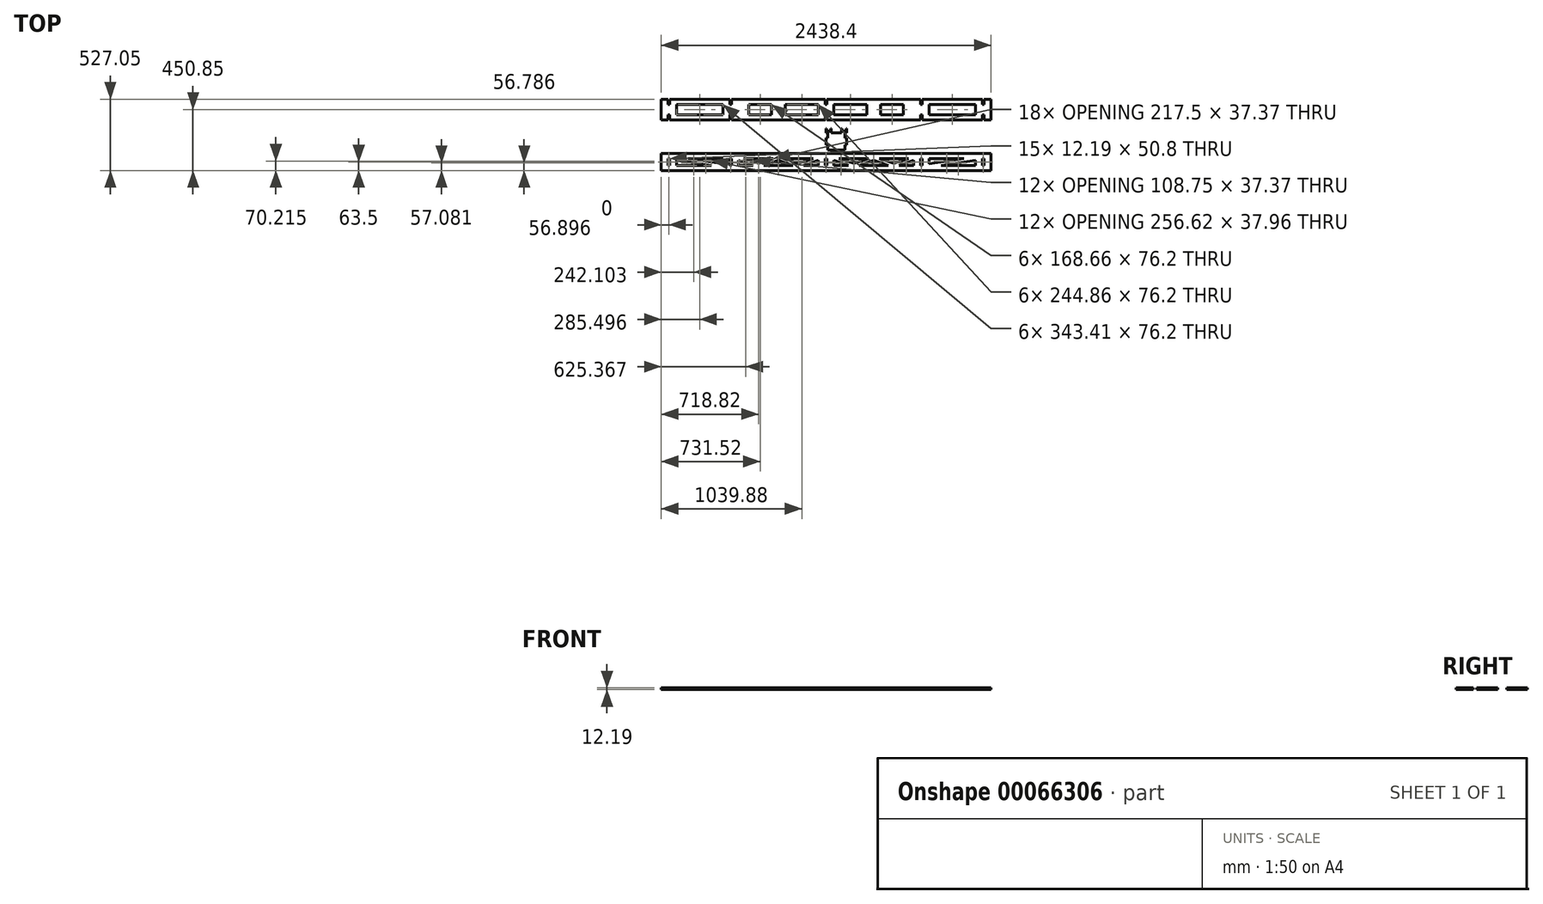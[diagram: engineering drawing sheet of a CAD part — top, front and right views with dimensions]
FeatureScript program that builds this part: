
annotation { "Feature Type Name" : "Feature", "Feature Type Description" : "" }
export const myFeature = defineFeature(function(context is Context, id is Id, definition is map)
    precondition{}
    {
        {
            var Q0;
            Q0=qCreatedBy(makeId("Top.planeOp"),FACE);
            var sketch = newSketch(context, id + "F0", { "sketchPlane" : qUnion([Q0])});
            skLineSegment(sketch, "E0.bottom", {"start": v(-1219.2, 44.45) * mm, "end": v(1219.2, 44.45) * mm});
            skLineSegment(sketch, "E0.top", {"start": v(-1219.2, -107.95) * mm, "end": v(1219.2, -107.95) * mm});
            skLineSegment(sketch, "E0.left", {"start": v(-1219.2, 44.45) * mm, "end": v(-1219.2, -107.95) * mm});
            skLineSegment(sketch, "E0.right", {"start": v(1219.2, 44.45) * mm, "end": v(1219.2, -107.95) * mm});
            skLineSegment(sketch, "E1", {"start": v(0, 44.45) * mm, "end": v(0, -107.95) * mm, "construction": true});
            skLineSegment(sketch, "E2.0", {"start": v(-6.1, 44.45) * mm, "end": v(-6.1, 6.35) * mm});
            skLineSegment(sketch, "E3.MirrorCS", {"start": v(6.1, 44.45) * mm, "end": v(6.1, 6.35) * mm});
            skLineSegment(sketch, "E4", {"start": v(-1219.2, -31.75) * mm, "end": v(-1168.4, -31.75) * mm, "construction": true});
            skLineSegment(sketch, "E5", {"start": v(-1219.2, -31.75) * mm, "end": v(-711.2, -31.75) * mm, "construction": true});
            skLineSegment(sketch, "E6", {"start": v(-711.2, 44.45) * mm, "end": v(-711.2, 6.35) * mm});
            skLineSegment(sketch, "E7", {"start": v(-1168.4, 44.45) * mm, "end": v(-1168.4, 6.35) * mm});
            skLineSegment(sketch, "E8.0", {"start": v(-1156.2, 44.45) * mm, "end": v(-1156.2, 6.35) * mm});
            skLineSegment(sketch, "E9.0", {"start": v(-699, 44.45) * mm, "end": v(-699, 6.35) * mm});
            skLineSegment(sketch, "E10.MirrorCS", {"start": v(699, 44.45) * mm, "end": v(699, 6.35) * mm});
            skLineSegment(sketch, "E11.MirrorCS", {"start": v(711.2, 44.45) * mm, "end": v(711.2, 6.35) * mm});
            skLineSegment(sketch, "E12.MirrorCS", {"start": v(1168.4, 44.45) * mm, "end": v(1168.4, 6.35) * mm});
            skLineSegment(sketch, "E13.MirrorCS", {"start": v(1156.2, 44.45) * mm, "end": v(1156.2, 6.35) * mm});
            skLineSegment(sketch, "E14", {"start": v(-1219.2, -31.75) * mm, "end": v(1219.2, -31.75) * mm, "construction": true});
            skLineSegment(sketch, "E15.0", {"start": v(-1219.2, 6.35) * mm, "end": v(1219.2, 6.35) * mm, "construction": true});
            skLineSegment(sketch, "E16.MirrorCS", {"start": v(-1219.2, -69.85) * mm, "end": v(1219.2, -69.85) * mm, "construction": true});
            skLineSegment(sketch, "E17", {"start": v(-1168.4, 6.35) * mm, "end": v(-1156.2, 6.35) * mm});
            skLineSegment(sketch, "E18", {"start": v(-711.2, 6.35) * mm, "end": v(-699, 6.35) * mm});
            skLineSegment(sketch, "E19", {"start": v(-6.1, 6.35) * mm, "end": v(6.1, 6.35) * mm});
            skLineSegment(sketch, "E20.MirrorCS", {"start": v(1168.4, 6.35) * mm, "end": v(1156.2, 6.35) * mm});
            skLineSegment(sketch, "E21.MirrorCS", {"start": v(711.2, 6.35) * mm, "end": v(699, 6.35) * mm});
            skLineSegment(sketch, "E22.MirrorCS", {"start": v(1168.4, -69.85) * mm, "end": v(1156.2, -69.85) * mm});
            skLineSegment(sketch, "E23.MirrorCS", {"start": v(-1168.4, -69.85) * mm, "end": v(-1156.2, -69.85) * mm});
            skLineSegment(sketch, "E24.MirrorCS", {"start": v(-6.1, -69.85) * mm, "end": v(6.1, -69.85) * mm});
            skLineSegment(sketch, "E25.MirrorCS", {"start": v(-711.2, -69.85) * mm, "end": v(-699, -69.85) * mm});
            skLineSegment(sketch, "E26.MirrorCS", {"start": v(711.2, -69.85) * mm, "end": v(699, -69.85) * mm});
            skLineSegment(sketch, "E27.0", {"start": v(-1105.4, 6.35) * mm, "end": v(-1105.4, -69.85) * mm});
            skLineSegment(sketch, "E28.0", {"start": v(-762, 6.35) * mm, "end": v(-762, -69.85) * mm});
            skLineSegment(sketch, "E29.0", {"start": v(-648.2, 6.35) * mm, "end": v(-648.2, -69.85) * mm, "construction": true});
            skLineSegment(sketch, "E30.0", {"start": v(-56.9, 6.35) * mm, "end": v(-56.9, -69.85) * mm});
            skLineSegment(sketch, "E31.0", {"start": v(56.9, 6.35) * mm, "end": v(56.9, -69.85) * mm});
            skLineSegment(sketch, "E32.0", {"start": v(648.2, 6.35) * mm, "end": v(648.2, -69.85) * mm});
            skLineSegment(sketch, "E33.0", {"start": v(762, 6.35) * mm, "end": v(762, -69.85) * mm});
            skLineSegment(sketch, "E34.0", {"start": v(1105.4, 6.35) * mm, "end": v(1105.4, -69.85) * mm});
            skLineSegment(sketch, "E35", {"start": v(-699, 110.18) * mm, "end": v(-6.1, 110.18) * mm, "construction": true});
            skLineSegment(sketch, "E36", {"start": v(-352.55, -69.85) * mm, "end": v(-352.55, 6.35) * mm, "construction": true});
            skPoint(sketch, "E36.startSnap0", {"position": v(-352.55, 110.18) * mm});
            skLineSegment(sketch, "E37.0", {"start": v(-403.35, -69.85) * mm, "end": v(-403.35, 6.35) * mm});
            skLineSegment(sketch, "E38.0", {"start": v(-301.75, -69.85) * mm, "end": v(-301.75, 6.35) * mm});
            skLineSegment(sketch, "E39", {"start": v(-1105.4, 6.35) * mm, "end": v(-762, 6.35) * mm});
            skLineSegment(sketch, "E40", {"start": v(-762, -69.85) * mm, "end": v(-1105.4, -69.85) * mm});
            skLineSegment(sketch, "E41", {"start": v(-648.2, 6.35) * mm, "end": v(-572, 6.35) * mm, "construction": true});
            skLineSegment(sketch, "E42", {"start": v(-301.75, 6.35) * mm, "end": v(-56.9, 6.35) * mm});
            skLineSegment(sketch, "E43", {"start": v(-56.9, -69.85) * mm, "end": v(-301.75, -69.85) * mm});
            skLineSegment(sketch, "E44", {"start": v(-403.35, -69.85) * mm, "end": v(-572, -69.85) * mm});
            skLineSegment(sketch, "E45.MirrorCS", {"start": v(403.35, -69.85) * mm, "end": v(648.2, -69.85) * mm});
            skLineSegment(sketch, "E46.MirrorCS", {"start": v(56.9, -69.85) * mm, "end": v(301.75, -69.85) * mm});
            skLineSegment(sketch, "E47.MirrorCS", {"start": v(301.75, 6.35) * mm, "end": v(56.9, 6.35) * mm});
            skLineSegment(sketch, "E48.MirrorCS", {"start": v(301.75, -69.85) * mm, "end": v(301.75, 6.35) * mm});
            skLineSegment(sketch, "E49.MirrorCS", {"start": v(403.35, -69.85) * mm, "end": v(403.35, 6.35) * mm});
            skLineSegment(sketch, "E50.MirrorCS", {"start": v(648.2, 6.35) * mm, "end": v(403.35, 6.35) * mm});
            skLineSegment(sketch, "E51.MirrorCS", {"start": v(1105.4, 6.35) * mm, "end": v(762, 6.35) * mm});
            skLineSegment(sketch, "E52.MirrorCS", {"start": v(762, -69.85) * mm, "end": v(1105.4, -69.85) * mm});
            skLineSegment(sketch, "E53.trimOffspring", {"start": v(699, -69.85) * mm, "end": v(699, -107.95) * mm});
            skLineSegment(sketch, "E54.trimOffspring", {"start": v(711.2, -69.85) * mm, "end": v(711.2, -107.95) * mm});
            skLineSegment(sketch, "E55.trimOffspring", {"start": v(1156.2, -69.85) * mm, "end": v(1156.2, -107.95) * mm});
            skLineSegment(sketch, "E56.trimOffspring", {"start": v(1168.4, -69.85) * mm, "end": v(1168.4, -107.95) * mm});
            skLineSegment(sketch, "E57.trimOffspring", {"start": v(-6.1, -69.85) * mm, "end": v(-6.1, -107.95) * mm});
            skLineSegment(sketch, "E58.trimOffspring", {"start": v(6.1, -69.85) * mm, "end": v(6.1, -107.95) * mm});
            skLineSegment(sketch, "E59.trimOffspring", {"start": v(-1168.4, -69.85) * mm, "end": v(-1168.4, -107.95) * mm});
            skLineSegment(sketch, "E60.trimOffspring", {"start": v(-1156.2, -69.85) * mm, "end": v(-1156.2, -107.95) * mm});
            skLineSegment(sketch, "E61.trimOffspring", {"start": v(-711.2, -69.85) * mm, "end": v(-711.2, -107.95) * mm});
            skLineSegment(sketch, "E62.trimOffspring", {"start": v(-699, -69.85) * mm, "end": v(-699, -107.95) * mm});
            skLineSegment(sketch, "E63.bottom", {"start": v(38.1, -203.2) * mm, "end": v(114.3, -203.2) * mm});
            skLineSegment(sketch, "E63.top", {"start": v(12.2, -330.2) * mm, "end": v(140.2, -330.2) * mm});
            skLineSegment(sketch, "E63.left", {"start": v(0, -241.3) * mm, "end": v(0, -292.1) * mm});
            skLineSegment(sketch, "E63.right", {"start": v(152.4, -241.3) * mm, "end": v(152.4, -292.1) * mm});
            skLineSegment(sketch, "E64.top", {"start": v(0, -174.18) * mm, "end": v(2.22, -174.18) * mm});
            skLineSegment(sketch, "E64.left", {"start": v(0, -203.2) * mm, "end": v(0, -174.18) * mm});
            skLineSegment(sketch, "E64.right", {"start": v(38.1, -203.2) * mm, "end": v(38.1, -174.18) * mm});
            skArc(sketch, "E65", {"start": v(2.22, -174.18) * mm, "mid": v(19.05, -191) * mm, "end": v(35.88, -174.18) * mm});
            skLineSegment(sketch, "E66.trimOffspring", {"start": v(35.88, -174.18) * mm, "end": v(38.1, -174.18) * mm});
            skLineSegment(sketch, "E67.bottom", {"start": v(0, -203.2) * mm, "end": v(12.2, -203.2) * mm});
            skLineSegment(sketch, "E67.top", {"start": v(0, -241.3) * mm, "end": v(12.2, -241.3) * mm});
            skLineSegment(sketch, "E67.right", {"start": v(12.2, -203.2) * mm, "end": v(12.2, -241.3) * mm});
            skLineSegment(sketch, "E68", {"start": v(0, -266.7) * mm, "end": v(152.4, -266.7) * mm, "construction": true});
            skLineSegment(sketch, "E69", {"start": v(152.4, -266.7) * mm, "end": v(76.2, -330.2) * mm, "construction": true});
            skLineSegment(sketch, "E70", {"start": v(76.2, -330.2) * mm, "end": v(76.2, -203.2) * mm, "construction": true});
            skLineSegment(sketch, "E71.MirrorCS", {"start": v(12.2, -330.2) * mm, "end": v(12.2, -292.1) * mm});
            skLineSegment(sketch, "E72.MirrorCS", {"start": v(0, -292.1) * mm, "end": v(12.2, -292.1) * mm});
            skLineSegment(sketch, "E73.MirrorCS", {"start": v(152.4, -203.2) * mm, "end": v(140.2, -203.2) * mm});
            skLineSegment(sketch, "E74.MirrorCS", {"start": v(140.2, -330.2) * mm, "end": v(140.2, -292.1) * mm});
            skLineSegment(sketch, "E75.MirrorCS", {"start": v(152.4, -241.3) * mm, "end": v(140.2, -241.3) * mm});
            skLineSegment(sketch, "E76.MirrorCS", {"start": v(140.2, -203.2) * mm, "end": v(140.2, -241.3) * mm});
            skLineSegment(sketch, "E77.MirrorCS", {"start": v(152.4, -292.1) * mm, "end": v(140.2, -292.1) * mm});
            skLineSegment(sketch, "E78.MirrorCS", {"start": v(114.3, -203.2) * mm, "end": v(114.3, -174.18) * mm});
            skArc(sketch, "E79.MirrorCS", {"start": v(150.18, -174.18) * mm, "mid": v(133.35, -191) * mm, "end": v(116.52, -174.18) * mm});
            skLineSegment(sketch, "E80.MirrorCS", {"start": v(116.52, -174.18) * mm, "end": v(114.3, -174.18) * mm});
            skLineSegment(sketch, "E81.MirrorCS", {"start": v(152.4, -174.18) * mm, "end": v(150.18, -174.18) * mm});
            skLineSegment(sketch, "E82.MirrorCS", {"start": v(152.4, -203.2) * mm, "end": v(152.4, -174.18) * mm});
            skPoint(sketch, "E83.MirrorCS.start.orphan", {"position": v(0, -330.2) * mm});
            skPoint(sketch, "E84.trimOffspring.end.orphan", {"position": v(152.4, -203.2) * mm});
            skPoint(sketch, "E85.MirrorCS.start.orphan", {"position": v(152.4, -330.2) * mm});
            skLineSegment(sketch, "E86.bottom", {"start": v(-1219.2, -355.6) * mm, "end": v(1219.2, -355.6) * mm});
            skLineSegment(sketch, "E86.top", {"start": v(-1219.2, -482.6) * mm, "end": v(1219.2, -482.6) * mm});
            skLineSegment(sketch, "E86.left", {"start": v(-1219.2, -355.6) * mm, "end": v(-1219.2, -482.6) * mm});
            skLineSegment(sketch, "E86.right", {"start": v(1219.2, -355.6) * mm, "end": v(1219.2, -482.6) * mm});
            skLineSegment(sketch, "E87.bottom", {"start": v(-1168.4, -355.6) * mm, "end": v(-1156.2, -355.6) * mm, "construction": true});
            skLineSegment(sketch, "E87.top", {"start": v(-1168.4, -393.7) * mm, "end": v(-1156.2, -393.7) * mm});
            skLineSegment(sketch, "E87.left", {"start": v(-1168.4, -355.6) * mm, "end": v(-1168.4, -393.7) * mm, "construction": true});
            skLineSegment(sketch, "E87.right", {"start": v(-1156.2, -355.6) * mm, "end": v(-1156.2, -393.7) * mm, "construction": true});
            skLineSegment(sketch, "E88", {"start": v(-1168.4, -393.7) * mm, "end": v(-1168.4, -444.5) * mm});
            skLineSegment(sketch, "E89", {"start": v(-1168.4, -444.5) * mm, "end": v(-1156.2, -444.5) * mm});
            skLineSegment(sketch, "E90", {"start": v(-1156.2, -444.5) * mm, "end": v(-1156.2, -393.7) * mm});
            skLineSegment(sketch, "E91", {"start": v(-1156.2, -241.75) * mm, "end": v(-711.2, -241.75) * mm, "construction": true});
            skLineSegment(sketch, "E92", {"start": v(-933.7, -241.75) * mm, "end": v(-933.7, -204.74) * mm, "construction": true});
            skLineSegment(sketch, "E93", {"start": v(-699, -247.2) * mm, "end": v(-6.1, -247.2) * mm, "construction": true});
            skLineSegment(sketch, "E94", {"start": v(-352.55, -247.2) * mm, "end": v(-352.55, -185.08) * mm, "construction": true});
            skLineSegment(sketch, "E95.MirrorCS", {"start": v(-699, -393.7) * mm, "end": v(-711.2, -393.7) * mm});
            skLineSegment(sketch, "E96.MirrorCS", {"start": v(-699, -393.7) * mm, "end": v(-699, -444.5) * mm});
            skLineSegment(sketch, "E97.MirrorCS", {"start": v(-711.2, -444.5) * mm, "end": v(-711.2, -393.7) * mm});
            skLineSegment(sketch, "E98.MirrorCS", {"start": v(-699, -444.5) * mm, "end": v(-711.2, -444.5) * mm});
            skLineSegment(sketch, "E99.MirrorCS", {"start": v(-6.1, -444.5) * mm, "end": v(6.1, -444.5) * mm});
            skLineSegment(sketch, "E100.MirrorCS", {"start": v(-6.1, -393.7) * mm, "end": v(6.1, -393.7) * mm});
            skLineSegment(sketch, "E101.MirrorCS", {"start": v(-6.1, -393.7) * mm, "end": v(-6.1, -444.5) * mm});
            skLineSegment(sketch, "E102.MirrorCS", {"start": v(6.1, -444.5) * mm, "end": v(6.1, -393.7) * mm});
            skLineSegment(sketch, "E103.MirrorCS", {"start": v(1168.4, -393.7) * mm, "end": v(1156.2, -393.7) * mm});
            skLineSegment(sketch, "E104.MirrorCS", {"start": v(1168.4, -393.7) * mm, "end": v(1168.4, -444.5) * mm});
            skLineSegment(sketch, "E105.MirrorCS", {"start": v(1168.4, -444.5) * mm, "end": v(1156.2, -444.5) * mm});
            skLineSegment(sketch, "E106.MirrorCS", {"start": v(1156.2, -444.5) * mm, "end": v(1156.2, -393.7) * mm});
            skLineSegment(sketch, "E107.MirrorCS", {"start": v(699, -444.5) * mm, "end": v(711.2, -444.5) * mm});
            skLineSegment(sketch, "E108.MirrorCS", {"start": v(699, -393.7) * mm, "end": v(711.2, -393.7) * mm});
            skLineSegment(sketch, "E109.MirrorCS", {"start": v(711.2, -444.5) * mm, "end": v(711.2, -393.7) * mm});
            skLineSegment(sketch, "E110.MirrorCS", {"start": v(699, -393.7) * mm, "end": v(699, -444.5) * mm});
            skLineSegment(sketch, "E111", {"start": v(-1018.62, -393.7) * mm, "end": v(-762, -393.7) * mm});
            skLineSegment(sketch, "E112", {"start": v(-762, -393.7) * mm, "end": v(-762, -431.66) * mm});
            skLineSegment(sketch, "E113", {"start": v(-848.79, -444.5) * mm, "end": v(-1105.4, -444.5) * mm});
            skLineSegment(sketch, "E114", {"start": v(-1105.4, -444.5) * mm, "end": v(-1105.4, -406.54) * mm});
            skLineSegment(sketch, "E115", {"start": v(-648.2, -407.13) * mm, "end": v(-648.2, -444.5) * mm});
            skLineSegment(sketch, "E116", {"start": v(-648.2, -444.5) * mm, "end": v(-539.46, -444.5) * mm});
            skLineSegment(sketch, "E117", {"start": v(-56.9, -444.5) * mm, "end": v(-56.9, -407.13) * mm});
            skLineSegment(sketch, "E118", {"start": v(-95.97, -393.7) * mm, "end": v(-313.47, -393.7) * mm});
            skLineSegment(sketch, "E119", {"start": v(-1105.4, -393.7) * mm, "end": v(-762, -444.5) * mm, "construction": true});
            skPoint(sketch, "E120.endSnap0", {"position": v(-525.78, -69.85) * mm});
            skPoint(sketch, "E121.endSnap0", {"position": v(-179.32, -69.85) * mm});
            skLineSegment(sketch, "E122", {"start": v(-352.55, -393.7) * mm, "end": v(-352.55, -444.5) * mm, "construction": true});
            skLineSegment(sketch, "E123", {"start": v(-352.55, -444.5) * mm, "end": v(-243.8, -444.5) * mm});
            skLineSegment(sketch, "E124", {"start": v(-648.2, -393.7) * mm, "end": v(-500.38, -444.5) * mm, "construction": true});
            skLineSegment(sketch, "E125", {"start": v(-500.38, -444.5) * mm, "end": v(-352.55, -393.7) * mm, "construction": true});
            skLineSegment(sketch, "E126", {"start": v(-352.55, -393.7) * mm, "end": v(-204.72, -444.5) * mm, "construction": true});
            skLineSegment(sketch, "E127", {"start": v(-204.72, -444.5) * mm, "end": v(-56.9, -393.7) * mm, "construction": true});
            skLineSegment(sketch, "E128.0", {"start": v(-1105.4, -406.54) * mm, "end": v(-848.79, -444.5) * mm});
            skLineSegment(sketch, "E129.0", {"start": v(-1018.62, -393.7) * mm, "end": v(-762, -431.66) * mm});
            skLineSegment(sketch, "E130.0", {"start": v(-609.13, -393.7) * mm, "end": v(-500.38, -431.07) * mm});
            skLineSegment(sketch, "E131.0", {"start": v(-648.2, -407.13) * mm, "end": v(-539.46, -444.5) * mm});
            skLineSegment(sketch, "E132.0", {"start": v(-500.38, -431.07) * mm, "end": v(-391.63, -393.7) * mm});
            skLineSegment(sketch, "E133.0", {"start": v(-461.3, -444.5) * mm, "end": v(-352.55, -407.13) * mm});
            skLineSegment(sketch, "E134.0", {"start": v(-313.47, -393.7) * mm, "end": v(-204.72, -431.07) * mm});
            skLineSegment(sketch, "E135.0", {"start": v(-352.55, -407.13) * mm, "end": v(-243.8, -444.5) * mm});
            skLineSegment(sketch, "E136.0", {"start": v(-204.72, -431.07) * mm, "end": v(-95.97, -393.7) * mm});
            skLineSegment(sketch, "E137.0", {"start": v(-165.65, -444.5) * mm, "end": v(-56.9, -407.13) * mm});
            skLineSegment(sketch, "E138.trimOffspring", {"start": v(-461.3, -444.5) * mm, "end": v(-352.55, -444.5) * mm});
            skLineSegment(sketch, "E139.trimOffspring", {"start": v(-165.65, -444.5) * mm, "end": v(-56.9, -444.5) * mm});
            skLineSegment(sketch, "E140.trimOffspring", {"start": v(-391.63, -393.7) * mm, "end": v(-609.13, -393.7) * mm});
            skLineSegment(sketch, "E141.MirrorCS", {"start": v(56.9, -444.5) * mm, "end": v(56.9, -407.13) * mm});
            skLineSegment(sketch, "E142.MirrorCS", {"start": v(313.47, -393.7) * mm, "end": v(204.72, -431.07) * mm});
            skLineSegment(sketch, "E143.MirrorCS", {"start": v(648.2, -444.5) * mm, "end": v(539.46, -444.5) * mm});
            skLineSegment(sketch, "E144.MirrorCS", {"start": v(165.65, -444.5) * mm, "end": v(56.9, -407.13) * mm});
            skLineSegment(sketch, "E145.MirrorCS", {"start": v(95.97, -393.7) * mm, "end": v(313.47, -393.7) * mm});
            skLineSegment(sketch, "E146.MirrorCS", {"start": v(204.72, -431.07) * mm, "end": v(95.97, -393.7) * mm});
            skLineSegment(sketch, "E147.MirrorCS", {"start": v(461.3, -444.5) * mm, "end": v(352.55, -444.5) * mm});
            skLineSegment(sketch, "E148.MirrorCS", {"start": v(352.55, -393.7) * mm, "end": v(352.55, -444.5) * mm, "construction": true});
            skLineSegment(sketch, "E149.MirrorCS", {"start": v(204.72, -444.5) * mm, "end": v(56.9, -393.7) * mm, "construction": true});
            skLineSegment(sketch, "E150.MirrorCS", {"start": v(648.2, -407.13) * mm, "end": v(648.2, -444.5) * mm});
            skLineSegment(sketch, "E151.MirrorCS", {"start": v(461.3, -444.5) * mm, "end": v(352.55, -407.13) * mm});
            skLineSegment(sketch, "E152.MirrorCS", {"start": v(352.55, -393.7) * mm, "end": v(204.72, -444.5) * mm, "construction": true});
            skLineSegment(sketch, "E153.MirrorCS", {"start": v(165.65, -444.5) * mm, "end": v(56.9, -444.5) * mm});
            skLineSegment(sketch, "E154.MirrorCS", {"start": v(352.55, -444.5) * mm, "end": v(243.8, -444.5) * mm});
            skLineSegment(sketch, "E155.MirrorCS", {"start": v(500.38, -431.07) * mm, "end": v(391.63, -393.7) * mm});
            skLineSegment(sketch, "E156.MirrorCS", {"start": v(352.55, -407.13) * mm, "end": v(243.8, -444.5) * mm});
            skLineSegment(sketch, "E157.MirrorCS", {"start": v(609.13, -393.7) * mm, "end": v(500.38, -431.07) * mm});
            skLineSegment(sketch, "E158.MirrorCS", {"start": v(391.63, -393.7) * mm, "end": v(609.13, -393.7) * mm});
            skLineSegment(sketch, "E159.MirrorCS", {"start": v(648.2, -393.7) * mm, "end": v(500.38, -444.5) * mm, "construction": true});
            skLineSegment(sketch, "E160.MirrorCS", {"start": v(648.2, -407.13) * mm, "end": v(539.46, -444.5) * mm});
            skLineSegment(sketch, "E161.MirrorCS", {"start": v(1105.4, -393.7) * mm, "end": v(762, -444.5) * mm, "construction": true});
            skLineSegment(sketch, "E162.MirrorCS", {"start": v(500.38, -444.5) * mm, "end": v(352.55, -393.7) * mm, "construction": true});
            skLineSegment(sketch, "E163.MirrorCS", {"start": v(1105.4, -406.54) * mm, "end": v(848.79, -444.5) * mm});
            skLineSegment(sketch, "E164.MirrorCS", {"start": v(1105.4, -444.5) * mm, "end": v(1105.4, -406.54) * mm});
            skLineSegment(sketch, "E165.MirrorCS", {"start": v(1018.62, -393.7) * mm, "end": v(762, -393.7) * mm});
            skLineSegment(sketch, "E166.MirrorCS", {"start": v(762, -393.7) * mm, "end": v(762, -431.66) * mm});
            skLineSegment(sketch, "E167.MirrorCS", {"start": v(1018.62, -393.7) * mm, "end": v(762, -431.66) * mm});
            skLineSegment(sketch, "E168.MirrorCS", {"start": v(848.79, -444.5) * mm, "end": v(1105.4, -444.5) * mm});
            skLineSegment(sketch, "E169.bottom", {"start": v(-1219.2, 508) * mm, "end": v(1219.2, 508) * mm});
            skLineSegment(sketch, "E169.top", {"start": v(-1219.2, -711.2) * mm, "end": v(1219.2, -711.2) * mm});
            skLineSegment(sketch, "E169.left", {"start": v(-1219.2, 508) * mm, "end": v(-1219.2, -711.2) * mm});
            skLineSegment(sketch, "E169.right", {"start": v(1219.2, 508) * mm, "end": v(1219.2, -711.2) * mm});
            skLineSegment(sketch, "E170.top", {"start": v(-648.2, -69.85) * mm, "end": v(-572, -69.85) * mm, "construction": true});
            skLineSegment(sketch, "E170.right", {"start": v(-572, 6.35) * mm, "end": v(-572, -69.85) * mm});
            skLineSegment(sketch, "E171", {"start": v(-572, 6.35) * mm, "end": v(-403.35, 6.35) * mm});
            skLineSegment(sketch, "E172", {"start": v(-572, -69.85) * mm, "end": v(-648.2, -69.85) * mm, "construction": true});
            skLineSegment(sketch, "E173.bottom", {"start": v(648.2, 6.35) * mm, "end": v(572, 6.35) * mm, "construction": true});
            skLineSegment(sketch, "E173.top", {"start": v(648.2, -69.85) * mm, "end": v(572, -69.85) * mm, "construction": true});
            skLineSegment(sketch, "E173.left", {"start": v(648.2, 6.35) * mm, "end": v(648.2, -69.85) * mm, "construction": true});
            skLineSegment(sketch, "E173.right", {"start": v(572, 6.35) * mm, "end": v(572, -69.85) * mm});
            skSolve(sketch);
        }
        {
            var Q0;
            {var subQ10=sQuery(id+"F0.wireOp",EDGE,"E0.left");Q0=makeQuery(id+"F0.imprint","IMPRINT",FACE,{"disambiguationData":[TD([[makeQuery(id+"F0.imprint","IMPRINT",EDGE,{"derivedFrom":subQ10}),1.0]])]});}
            var Q1;
            Q1=makeQuery(id+"F0.imprint","IMPRINT",FACE,{"disambiguationData":[TD([[makeQuery(id+"F0.imprint","IMPRINT",EDGE,{"derivedFrom":sQuery(id+"F0.wireOp",EDGE,"E63.bottom")}),-1.0]])]});
            var Q2;
            Q2=makeQuery(id+"F0.imprint","IMPRINT",FACE,{"disambiguationData":[TD([[makeQuery(id+"F0.imprint","IMPRINT",EDGE,{"derivedFrom":sQuery(id+"F0.wireOp",EDGE,"E86.bottom")}),-1.0]])]});
            var Q3;
            {var subQ10=sQuery(id+"F0.wireOp",EDGE,"E2.0");Q3=makeQuery(id+"F0.imprint","IMPRINT",FACE,{"disambiguationData":[TD([[makeQuery(id+"F0.imprint","IMPRINT",EDGE,{"derivedFrom":subQ10}),-1.0]])]});}
            var Q4;
            {var subQ0=sQuery(id+"F0.wireOp",EDGE,"E32.0");Q4=makeQuery(id+"F0.imprint","IMPRINT",FACE,{"disambiguationData":[TD([[makeQuery(id+"F0.imprint","IMPRINT",EDGE,{"derivedFrom":subQ0}),-1.0]])]});}
            extrude(context, id + "F1", {"entities" : qUnion([Q0, Q1, Q2, Q3, Q4]), "depth" : 12.2 * mm});
        }
    });
